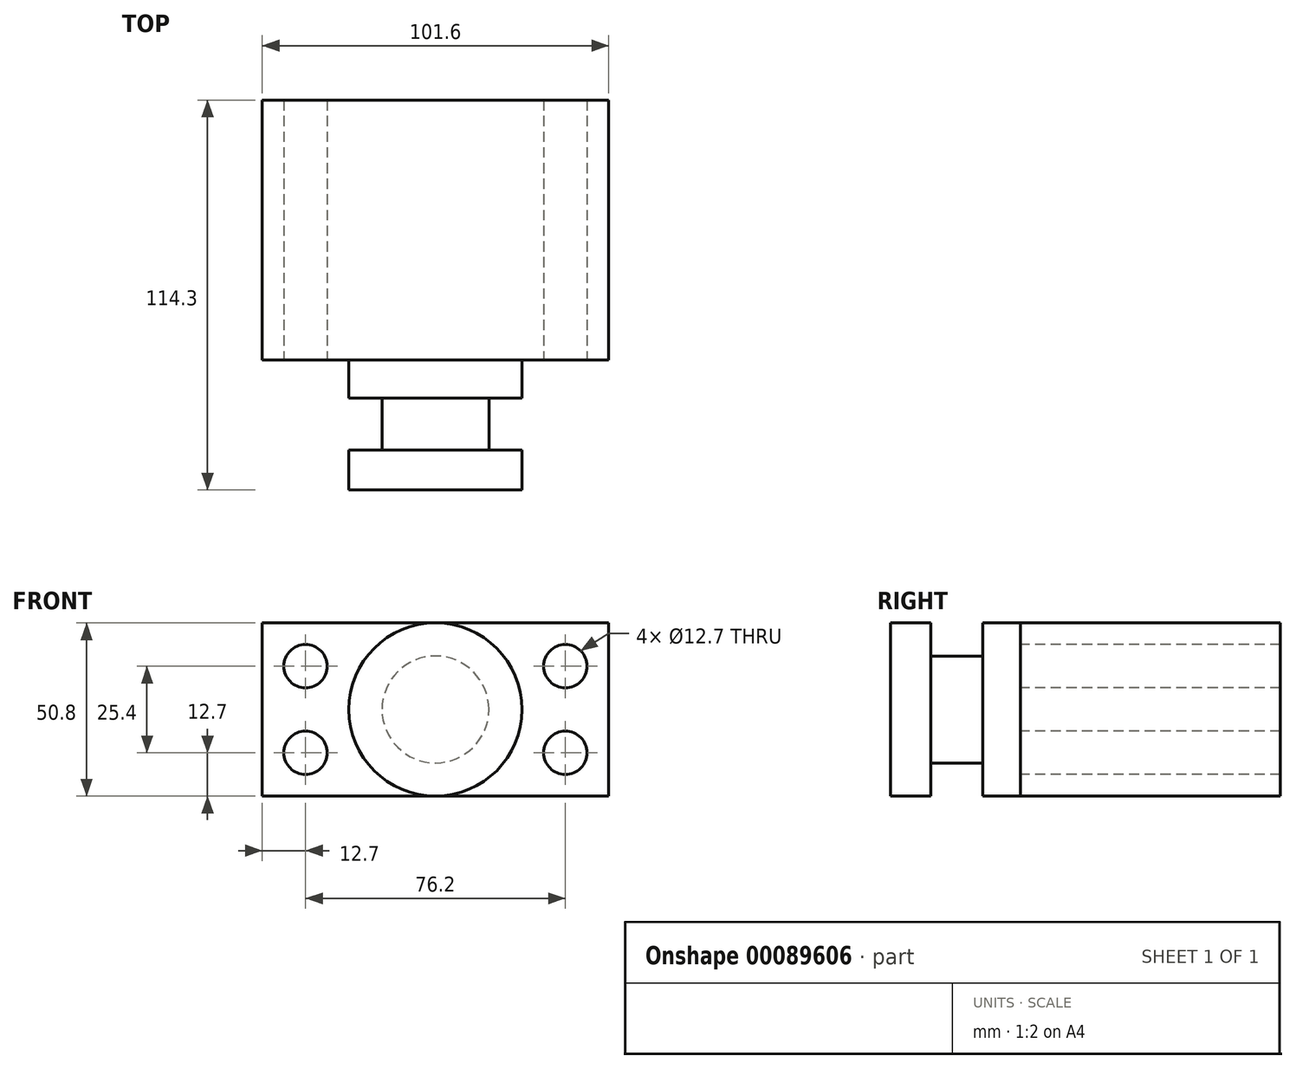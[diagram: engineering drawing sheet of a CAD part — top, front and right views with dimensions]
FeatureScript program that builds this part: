
annotation { "Feature Type Name" : "Feature", "Feature Type Description" : "" }
export const myFeature = defineFeature(function(context is Context, id is Id, definition is map)
    precondition{}
    {
        {
            var Q0;
            Q0=qCreatedBy(makeId("Front.planeOp"),FACE);
            var sketch = newSketch(context, id + "F0", { "sketchPlane" : qUnion([Q0])});
            skLineSegment(sketch, "E0", {"start": v(50.8, 25.4) * mm, "end": v(50.8, -25.4) * mm});
            skLineSegment(sketch, "E1", {"start": v(50.8, -25.4) * mm, "end": v(-50.8, -25.4) * mm});
            skLineSegment(sketch, "E2", {"start": v(-50.8, -25.4) * mm, "end": v(-50.8, 25.4) * mm});
            skLineSegment(sketch, "E3", {"start": v(-50.8, 25.4) * mm, "end": v(50.8, 25.4) * mm});
            skSolve(sketch);
        }
        {
            var Q0;
            Q0=makeQuery(id+"F0.imprint","IMPRINT",FACE,{"disambiguationData":[TD([[makeQuery(id+"F0.imprint","IMPRINT",EDGE,{"derivedFrom":sQuery(id+"F0.wireOp",EDGE,"E0")}),-1.0]])]});
            extrude(context, id + "F1", {"entities" : qUnion([Q0]), "depth" : 76.2 * mm});
        }
        {
            var Q0;
            Q0=makeQuery(id+"F1.opExtrude","CAP_FACE",FACE,{"disambiguationData":[OSD([sQuery(id+"F0.wireOp",EDGE,"E0"),sQuery(id+"F0.wireOp",EDGE,"E1"),sQuery(id+"F0.wireOp",EDGE,"E2"),sQuery(id+"F0.wireOp",EDGE,"E3")])],"isStart":false});
            var sketch = newSketch(context, id + "F2", { "sketchPlane" : qUnion([Q0])});
            skCircle(sketch, "E4", {"center": v(-38.1, 12.7) * mm, "radius": 6.35 * mm});
            skCircle(sketch, "E5", {"center": v(-38.1, -12.7) * mm, "radius": 6.35 * mm});
            skCircle(sketch, "E6", {"center": v(38.1, 12.7) * mm, "radius": 6.35 * mm});
            skCircle(sketch, "E7", {"center": v(38.1, -12.7) * mm, "radius": 6.35 * mm});
            skSolve(sketch);
        }
        {
            var Q0;
            Q0 = qSketchRegion(id + "F2", true);
            extrude(context, id + "F3", {"entities" : qUnion([Q0]), "operationType" : NewBodyOperationType.REMOVE, "endBound" : BoundingType.THROUGH_ALL, "oppositeDirection" : true, "depth" : 25.4 * mm});
        }
        {
            var Q0;
            Q0=qCreatedBy(makeId("Top.planeOp"),FACE);
            var sketch = newSketch(context, id + "F4", { "sketchPlane" : qUnion([Q0])});
            skLineSegment(sketch, "E8", {"start": v(-25.4, -114.3) * mm, "end": v(-25.4, -76.2) * mm});
            skLineSegment(sketch, "E9", {"start": v(-25.4, -76.2) * mm, "end": v(0, -76.2) * mm});
            skLineSegment(sketch, "E10", {"start": v(0, -76.2) * mm, "end": v(0, -114.3) * mm});
            skLineSegment(sketch, "E11", {"start": v(0, -114.3) * mm, "end": v(-25.4, -114.3) * mm});
            skSolve(sketch);
        }
        {
            var Q0;
            Q0 = qSketchRegion(id + "F4", true);
            var Q1;
            Q1=sQuery(id+"F4.wireOp",EDGE,"E10");
            revolve(context, id + "F5", {"operationType" : NewBodyOperationType.ADD, "entities" : qUnion([Q0]), "axis" : qUnion([Q1]), "revolveType" : RevolveType.FULL});
        }
        {
            var Q0;
            Q0=qCreatedBy(makeId("Top.planeOp"),FACE);
            var sketch = newSketch(context, id + "F6", { "sketchPlane" : qUnion([Q0])});
            skLineSegment(sketch, "E12", {"start": v(0, -123.86) * mm, "end": v(0, 0) * mm, "construction": true});
            skLineSegment(sketch, "E13", {"start": v(-25.5, -102.62) * mm, "end": v(-15.67, -102.62) * mm});
            skLineSegment(sketch, "E14", {"start": v(-15.67, -102.62) * mm, "end": v(-15.67, -87.3) * mm});
            skLineSegment(sketch, "E15", {"start": v(-15.67, -87.3) * mm, "end": v(-25.5, -87.3) * mm});
            skLineSegment(sketch, "E16", {"start": v(-25.5, -87.3) * mm, "end": v(-25.5, -102.62) * mm});
            skLineSegment(sketch, "E17", {"start": v(-25.4, -114.3) * mm, "end": v(-25.4, -76.2) * mm});
            skSolve(sketch);
        }
        {
            var Q0;
            Q0 = qSketchRegion(id + "F6", true);
            var Q1;
            Q1=sQuery(id+"F6.wireOp",EDGE,"E12");
            revolve(context, id + "F7", {"operationType" : NewBodyOperationType.REMOVE, "entities" : qUnion([Q0]), "axis" : qUnion([Q1]), "revolveType" : RevolveType.FULL, "oppositeDirection" : true});
        }
    });
